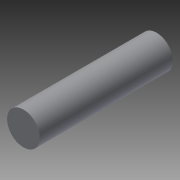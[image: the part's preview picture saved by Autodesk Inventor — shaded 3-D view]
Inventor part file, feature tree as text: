
AUTODESK INVENTOR PART (.ipt)
format: ipt  version: 2014 (Build 180170000, 170)  size: 69,120 bytes
history: native  units: in
note: dims shown in document units (in); Inventor stores cm internally (conversion verified against a paired STEP export)
features: extrude x1, sketch x1
ambient origin geometry x8: Origin, YZ Plane, XZ Plane, XY Plane, X Axis, Y Axis, Z Axis, Center Point
bodies: Solid1 (feature_tree)
feature tree (2):
  extrude  "Extrusion1"  Depth=10.0in TaperAngle=0.0deg
  sketch  "Sketch1"  dims[d0=2.462in d1=10.0in d2=0.0in]
